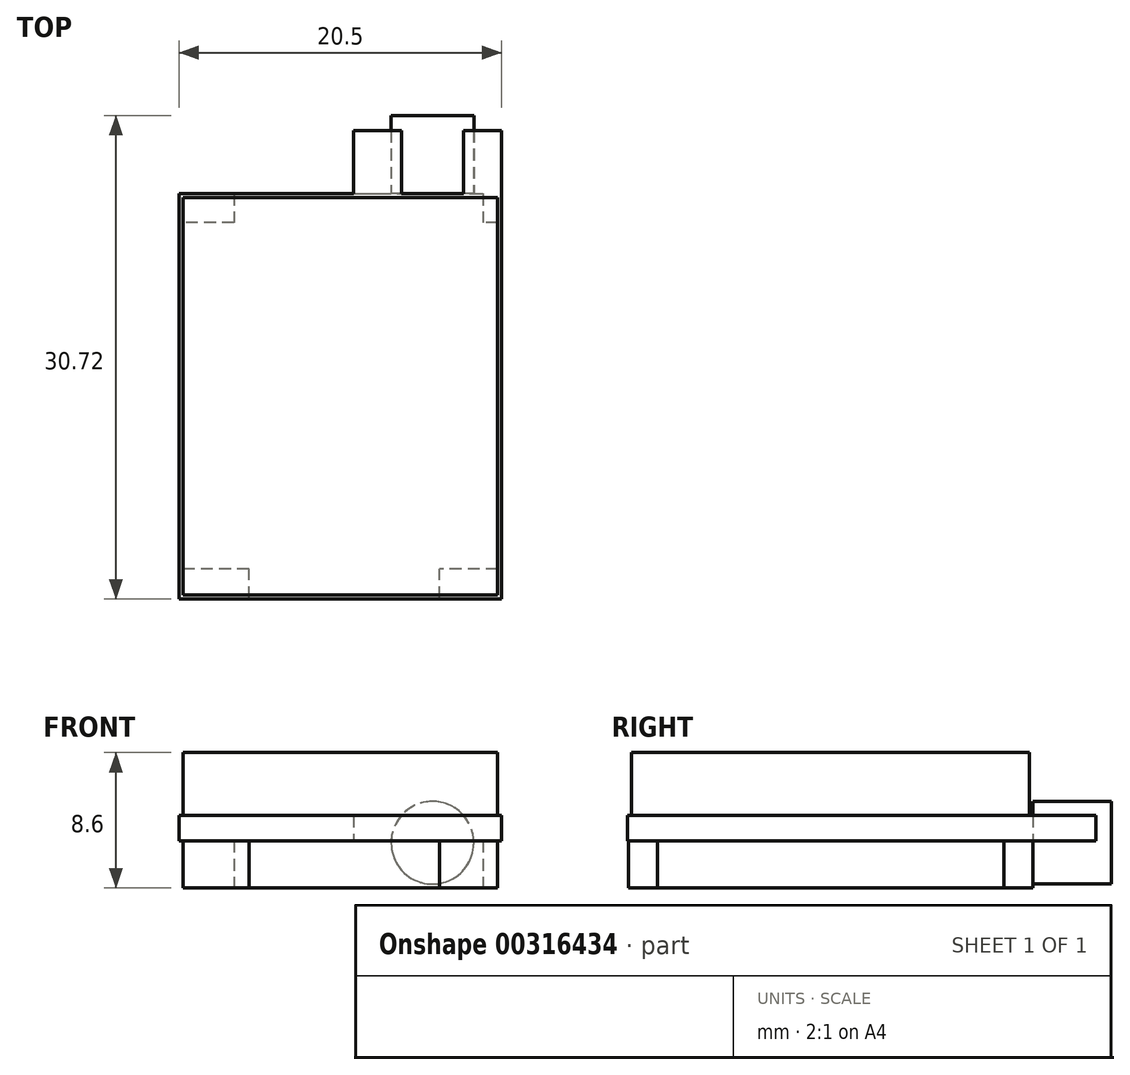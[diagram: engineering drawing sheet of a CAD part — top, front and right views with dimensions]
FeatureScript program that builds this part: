
annotation { "Feature Type Name" : "Feature", "Feature Type Description" : "" }
export const myFeature = defineFeature(function(context is Context, id is Id, definition is map)
    precondition{}
    {
        {
            var Q0;
            Q0=qCreatedBy(makeId("Top.planeOp"),FACE);
            cPlane(context, id + "F0", {"entities" : qUnion([Q0]), "cplaneType" : CPlaneType.OFFSET, "offset" : 3 * mm, "width" : 150 * mm, "height" : 150 * mm});
        }
        {
            var Q0;
            Q0=qCreatedBy(id+"F0.planeOp",FACE);
            var sketch = newSketch(context, id + "F1", { "sketchPlane" : qUnion([Q0])});
            skLineSegment(sketch, "E0.bottom", {"start": v(-10.25, 12.88) * mm, "end": v(10.25, 12.88) * mm});
            skLineSegment(sketch, "E0.top", {"start": v(-10.25, -12.88) * mm, "end": v(10.25, -12.88) * mm});
            skLineSegment(sketch, "E0.left", {"start": v(-10.25, 12.88) * mm, "end": v(-10.25, -12.88) * mm});
            skLineSegment(sketch, "E0.right", {"start": v(10.25, 12.88) * mm, "end": v(10.25, -12.88) * mm});
            skPoint(sketch, "E0.middle", {"position": v(0, 0) * mm});
            skLineSegment(sketch, "E1.bottom", {"start": v(0.85, 16.87) * mm, "end": v(10.25, 16.88) * mm});
            skLineSegment(sketch, "E1.top", {"start": v(0.85, 12.88) * mm, "end": v(10.25, 12.88) * mm});
            skLineSegment(sketch, "E1.left", {"start": v(0.85, 16.87) * mm, "end": v(0.85, 12.87) * mm});
            skLineSegment(sketch, "E1.right", {"start": v(10.25, 16.88) * mm, "end": v(10.25, 12.88) * mm});
            skPoint(sketch, "E1.middle", {"position": v(5.55, 14.87) * mm});
            skSolve(sketch);
        }
        {
            var Q0;
            Q0 = qSketchRegion(id + "F1", true);
            extrude(context, id + "F2", {"entities" : qUnion([Q0]), "depth" : 1.6 * mm});
        }
        {
            var Q0;
            Q0=qCreatedBy(makeId("Top.planeOp"),FACE);
            cPlane(context, id + "F3", {"entities" : qUnion([Q0]), "cplaneType" : CPlaneType.OFFSET, "offset" : 0 * mm, "width" : 150 * mm, "height" : 150 * mm});
        }
        {
            var Q0;
            Q0=qCreatedBy(id+"F3.planeOp",FACE);
            var sketch = newSketch(context, id + "F4", { "sketchPlane" : qUnion([Q0])});
            skLineSegment(sketch, "E2.bottom", {"start": v(10, 11.03) * mm, "end": v(-10, 11.03) * mm});
            skLineSegment(sketch, "E2.top", {"start": v(10, -10.97) * mm, "end": v(-10, -10.97) * mm});
            skLineSegment(sketch, "E2.left", {"start": v(10, 11.03) * mm, "end": v(10, -10.97) * mm});
            skLineSegment(sketch, "E2.right", {"start": v(-10, 11.03) * mm, "end": v(-10, -10.97) * mm});
            skPoint(sketch, "E2.middle", {"position": v(0, 0.03) * mm});
            skLineSegment(sketch, "E3.bottom", {"start": v(6.3, -12.83) * mm, "end": v(-5.8, -12.83) * mm});
            skLineSegment(sketch, "E3.top", {"start": v(6.3, -10.98) * mm, "end": v(-5.8, -10.98) * mm});
            skLineSegment(sketch, "E3.left", {"start": v(6.3, -12.83) * mm, "end": v(6.3, -10.98) * mm});
            skLineSegment(sketch, "E3.right", {"start": v(-5.8, -12.83) * mm, "end": v(-5.8, -10.98) * mm});
            skPoint(sketch, "E3.middle", {"position": v(0.25, -11.9) * mm});
            skLineSegment(sketch, "E4.bottom", {"start": v(-6.75, 12.88) * mm, "end": v(9.05, 12.88) * mm});
            skLineSegment(sketch, "E4.top", {"start": v(-6.75, 11.02) * mm, "end": v(9.05, 11.02) * mm});
            skLineSegment(sketch, "E4.left", {"start": v(-6.75, 12.88) * mm, "end": v(-6.75, 11.03) * mm});
            skLineSegment(sketch, "E4.right", {"start": v(9.05, 12.88) * mm, "end": v(9.05, 11.03) * mm});
            skSolve(sketch);
        }
        {
            var Q0;
            Q0 = qSketchRegion(id + "F4", true);
            extrude(context, id + "F5", {"entities" : qUnion([Q0]), "depth" : 3 * mm});
        }
        {
            var Q0;
            Q0=makeQuery(id+"F2.opExtrude","SWEPT_FACE",FACE,{"disambiguationData":[OSD([sQuery(id+"F1.wireOp",EDGE,"E0.bottom")])]});
            var sketch = newSketch(context, id + "F6", { "sketchPlane" : qUnion([Q0])});
            skCircle(sketch, "E5", {"center": v(-5.86, 2.88) * mm, "radius": 2.62 * mm});
            skSolve(sketch);
        }
        {
            var Q0;
            Q0 = qSketchRegion(id + "F6", true);
            extrude(context, id + "F7", {"entities" : qUnion([Q0]), "operationType" : NewBodyOperationType.ADD, "depth" : 4.96 * mm});
        }
        {
            var Q0;
            Q0=makeQuery(id+"F2.opExtrude","CAP_FACE",FACE,{"disambiguationData":[OSD([sQuery(id+"F1.wireOp",EDGE,"E0.bottom"),sQuery(id+"F1.wireOp",EDGE,"E0.top"),sQuery(id+"F1.wireOp",EDGE,"E0.left"),sQuery(id+"F1.wireOp",EDGE,"E0.right"),sQuery(id+"F1.wireOp",EDGE,"E1.bottom"),sQuery(id+"F1.wireOp",EDGE,"E1.left"),sQuery(id+"F1.wireOp",EDGE,"E1.right")])],"isStart":false});
            var sketch = newSketch(context, id + "F8", { "sketchPlane" : qUnion([Q0])});
            skLineSegment(sketch, "E6.bottom", {"start": v(-10, 12.62) * mm, "end": v(10, 12.62) * mm});
            skLineSegment(sketch, "E6.top", {"start": v(-10, -12.62) * mm, "end": v(10, -12.62) * mm});
            skLineSegment(sketch, "E6.left", {"start": v(-10, 12.62) * mm, "end": v(-10, -12.62) * mm});
            skLineSegment(sketch, "E6.right", {"start": v(10, 12.62) * mm, "end": v(10, -12.62) * mm});
            skSolve(sketch);
        }
        {
            var Q0;
            Q0 = qSketchRegion(id + "F8", true);
            extrude(context, id + "F9", {"entities" : qUnion([Q0]), "operationType" : NewBodyOperationType.ADD, "depth" : 4 * mm});
        }
    });
